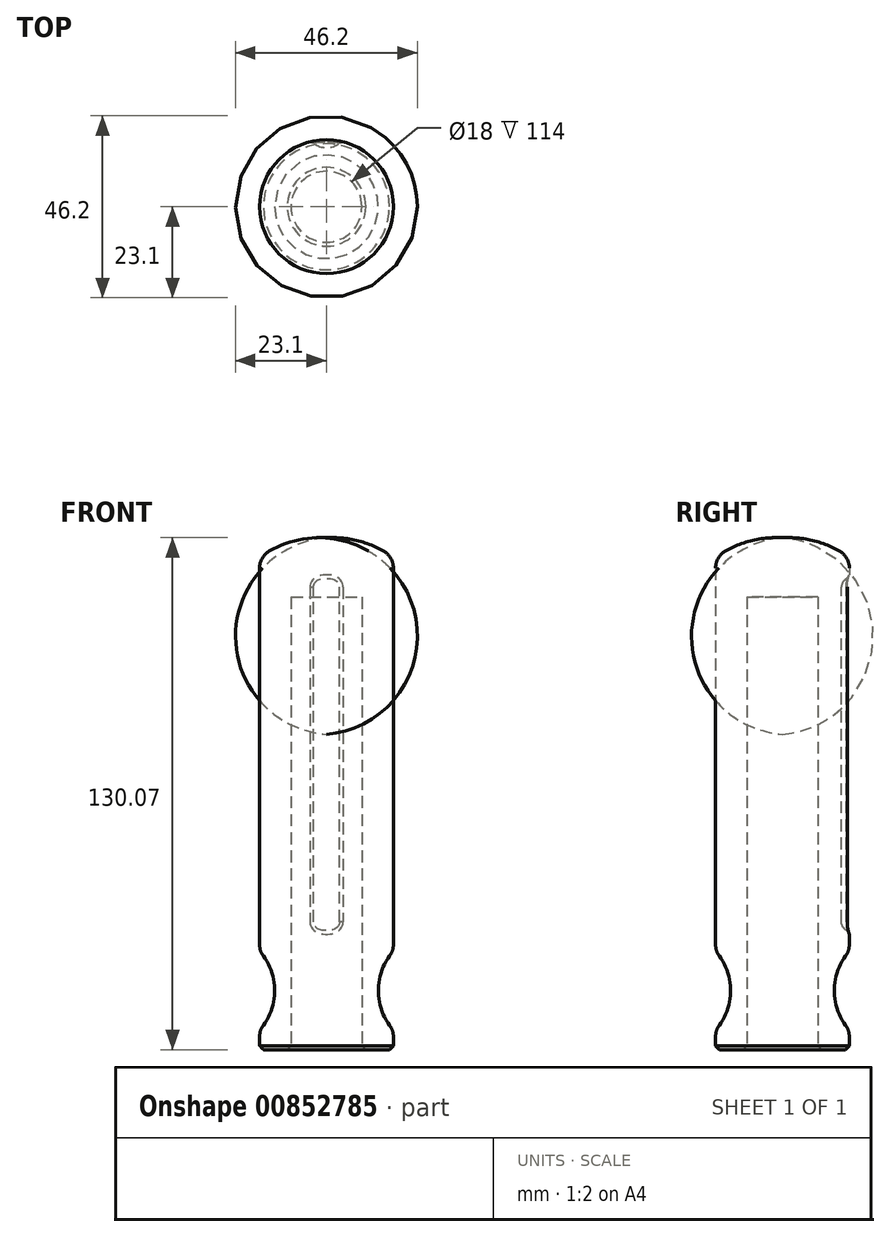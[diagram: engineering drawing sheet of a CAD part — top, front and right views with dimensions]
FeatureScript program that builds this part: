
annotation { "Feature Type Name" : "Feature", "Feature Type Description" : "" }
export const myFeature = defineFeature(function(context is Context, id is Id, definition is map)
    precondition{}
    {
        {
            var Q0;
            Q0=qCreatedBy(makeId("Front.planeOp"),FACE);
            var sketch = newSketch(context, id + "F0", { "sketchPlane" : qUnion([Q0])});
            skLineSegment(sketch, "E0", {"start": v(0, 0) * mm, "end": v(0, 115) * mm});
            skLineSegment(sketch, "E1", {"start": v(0, 115) * mm, "end": v(9, 115) * mm});
            skLineSegment(sketch, "E2", {"start": v(9, 115) * mm, "end": v(9, 0) * mm});
            skLineSegment(sketch, "E3", {"start": v(9, 0) * mm, "end": v(17, 0) * mm});
            skLineSegment(sketch, "E4", {"start": v(17, 25) * mm, "end": v(17, 125) * mm});
            skArc(sketch, "E5", {"start": v(17, 125) * mm, "mid": v(8.96, 129.06) * mm, "end": v(0, 130) * mm});
            skLineSegment(sketch, "E6", {"start": v(0, 115) * mm, "end": v(0, 130) * mm});
            skLineSegment(sketch, "E7", {"start": v(17, 0) * mm, "end": v(17, 5) * mm});
            skArc(sketch, "E8", {"start": v(17, 25) * mm, "mid": v(13.18, 15) * mm, "end": v(17, 5) * mm});
            skSolve(sketch);
        }
        {
            var Q0;
            Q0=makeQuery(id+"F0.imprint","IMPRINT",FACE,{"disambiguationData":[TD([[makeQuery(id+"F0.imprint","IMPRINT",EDGE,{"derivedFrom":sQuery(id+"F0.wireOp",EDGE,"E1")}),1.0]])]});
            var Q1;
            Q1=sQuery(id+"F0.wireOp",EDGE,"E6");
            revolve(context, id + "F1", {"surfaceOperationType" : NewSurfaceOperationType.NEW, "entities" : qUnion([Q0]), "axis" : qUnion([Q1]), "revolveType" : RevolveType.FULL});
        }
        {
            var Q0;
            Q0=qCreatedBy(makeId("Top.planeOp"),FACE);
            cPlane(context, id + "F2", {"entities" : qUnion([Q0]), "cplaneType" : CPlaneType.OFFSET, "offset" : 120 * mm, "width" : 150 * mm, "height" : 150 * mm});
        }
        {
            var Q0;
            Q0=qCreatedBy(id+"F2.planeOp",FACE);
            var sketch = newSketch(context, id + "F3", { "sketchPlane" : qUnion([Q0])});
            skCircle(sketch, "E9", {"center": v(0, 20) * mm, "radius": 5 * mm});
            skSolve(sketch);
        }
        {
            var Q0;
            Q0=makeQuery(id+"F3.imprint","IMPRINT",FACE,{"disambiguationData":[TD([[makeQuery(id+"F3.imprint","IMPRINT",EDGE,{"derivedFrom":sQuery(id+"F3.wireOp",EDGE,"E9")}),1.0]])]});
            extrude(context, id + "F4", {"entities" : qUnion([Q0]), "operationType" : NewBodyOperationType.REMOVE, "oppositeDirection" : true, "depth" : 90 * mm, "offsetDistance" : 25 * mm});
        }
        {
            var Q0;
            Q0=makeQuery(id+"F4.boolean.opBoolean","COPY",EDGE,{"derivedFrom":makeQuery(id+"F4.opExtrude","CAP_EDGE",EDGE,{"disambiguationData":[OSD([sQuery(id+"F3.wireOp",EDGE,"E9")])],"isStart":true})});
            var Q1;
            Q1=makeQuery(id+"F4.boolean.opBoolean","COPY",EDGE,{"derivedFrom":makeQuery(id+"F4.opExtrude","CAP_EDGE",EDGE,{"disambiguationData":[OSD([sQuery(id+"F3.wireOp",EDGE,"E9")])],"isStart":false})});
            fillet(context, id + "F5", {"entities" : qUnion([Q0, Q1]), "radius" : 2.5 * mm, "tangentPropagation" : true, "allowEdgeOverflow" : false});
        }
        {
            var Q0;
            Q0=makeQuery(id+"F4.boolean.opBoolean","INTERSECT",EDGE,{"disambiguationData":[OD(1.0)],"derivedFrom":[makeQuery(id+"F1.opRevolve","SWEPT_FACE",FACE,{"disambiguationData":[OSD([sQuery(id+"F0.wireOp",EDGE,"E4")])]}),makeQuery(id+"F4.opExtrude","SWEPT_FACE",FACE,{"disambiguationData":[OSD([sQuery(id+"F3.wireOp",EDGE,"E9")])]})]});
            chamfer(context, id + "F6", {"entities" : qUnion([Q0]), "width" : 1 * mm, "tangentPropagation" : true});
        }
        {
            var Q0;
            Q0=makeQuery(id+"F1.opRevolve","SWEPT_EDGE",EDGE,{"disambiguationData":[OSD([sQuery(id+"F0.wireOp",EDGE,"E4"),sQuery(id+"F0.wireOp",EDGE,"E5")])]});
            var Q1;
            Q1=makeQuery(id+"F1.opRevolve","SWEPT_EDGE",EDGE,{"disambiguationData":[OSD([sQuery(id+"F0.wireOp",EDGE,"E4"),sQuery(id+"F0.wireOp",EDGE,"E8")])]});
            var Q2;
            Q2=makeQuery(id+"F1.opRevolve","SWEPT_EDGE",EDGE,{"disambiguationData":[OSD([sQuery(id+"F0.wireOp",EDGE,"E7"),sQuery(id+"F0.wireOp",EDGE,"E8")])]});
            fillet(context, id + "F7", {"entities" : qUnion([Q0, Q1, Q2]), "radius" : 5 * mm, "tangentPropagation" : true, "allowEdgeOverflow" : false});
        }
        {
            var Q0;
            Q0=makeQuery(id+"F1.opRevolve","SWEPT_EDGE",EDGE,{"disambiguationData":[OSD([sQuery(id+"F0.wireOp",EDGE,"E2"),sQuery(id+"F0.wireOp",EDGE,"E3")])]});
            var Q1;
            Q1=makeQuery(id+"F1.opRevolve","SWEPT_EDGE",EDGE,{"disambiguationData":[OSD([sQuery(id+"F0.wireOp",EDGE,"E3"),sQuery(id+"F0.wireOp",EDGE,"E7")])]});
            chamfer(context, id + "F8", {"entities" : qUnion([Q0, Q1]), "width" : 1 * mm, "tangentPropagation" : true});
        }
    });
